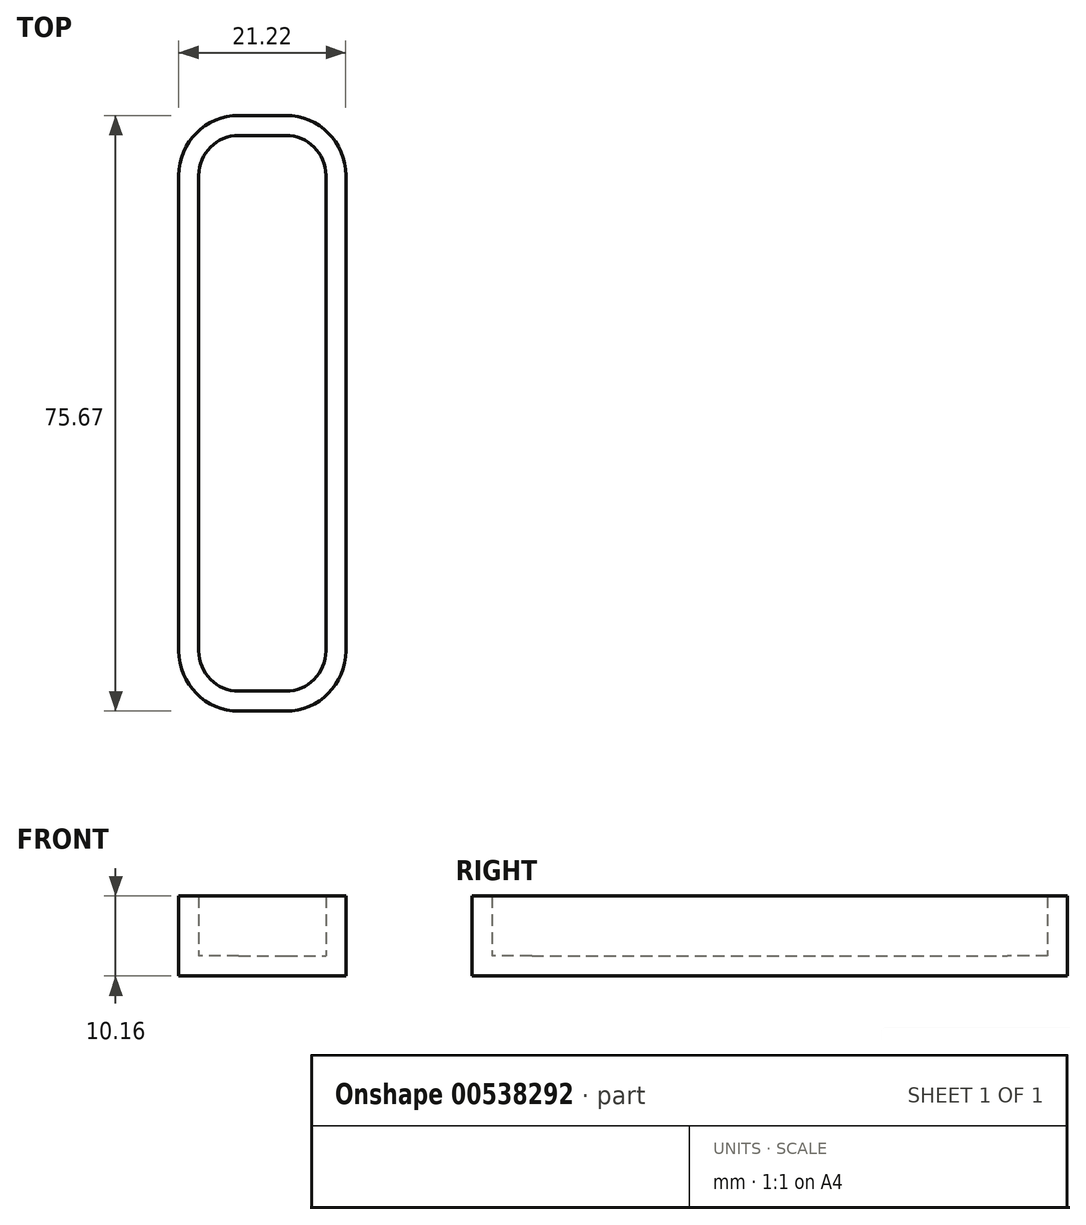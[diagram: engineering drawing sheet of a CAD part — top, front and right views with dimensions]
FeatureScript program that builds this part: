
annotation { "Feature Type Name" : "Feature", "Feature Type Description" : "" }
export const myFeature = defineFeature(function(context is Context, id is Id, definition is map)
    precondition{}
    {
        {
            var Q0;
            Q0=qCreatedBy(makeId("Top.planeOp"),FACE);
            var sketch = newSketch(context, id + "F0", { "sketchPlane" : qUnion([Q0])});
            skLineSegment(sketch, "E0.bottom", {"start": v(-143.26, -29.32) * mm, "end": v(-127.12, -29.32) * mm});
            skLineSegment(sketch, "E0.top", {"start": v(-143.26, 41.27) * mm, "end": v(-127.12, 41.27) * mm});
            skLineSegment(sketch, "E0.left", {"start": v(-143.26, -29.32) * mm, "end": v(-143.26, 41.27) * mm});
            skLineSegment(sketch, "E0.right", {"start": v(-127.12, -29.32) * mm, "end": v(-127.12, 41.27) * mm});
            skSolve(sketch);
        }
        {
            var Q0;
            Q0=makeQuery(id+"F0.imprint","IMPRINT",FACE,{"disambiguationData":[TD([[makeQuery(id+"F0.imprint","IMPRINT",EDGE,{"derivedFrom":sQuery(id+"F0.wireOp",EDGE,"E0.bottom")}),1.0]])]});
            extrude(context, id + "F1", {"entities" : qUnion([Q0]), "depth" : 7.62 * mm, "offsetDistance" : 25.4 * mm});
        }
        {
            var Q0;
            Q0=makeQuery(id+"F1.opExtrude","SWEPT_EDGE",EDGE,{"disambiguationData":[OSD([sQuery(id+"F0.wireOp",EDGE,"E0.bottom"),sQuery(id+"F0.wireOp",EDGE,"E0.left")])]});
            fillet(context, id + "F2", {"entities" : qUnion([Q0]), "radius" : 5.08 * mm, "tangentPropagation" : true, "allowEdgeOverflow" : false});
        }
        {
            var Q0;
            Q0=makeQuery(id+"F1.opExtrude","SWEPT_EDGE",EDGE,{"disambiguationData":[OSD([sQuery(id+"F0.wireOp",EDGE,"E0.bottom"),sQuery(id+"F0.wireOp",EDGE,"E0.right")])]});
            fillet(context, id + "F3", {"entities" : qUnion([Q0]), "radius" : 5.08 * mm, "tangentPropagation" : true, "allowEdgeOverflow" : false});
        }
        {
            var Q0;
            Q0=makeQuery(id+"F1.opExtrude","SWEPT_EDGE",EDGE,{"disambiguationData":[OSD([sQuery(id+"F0.wireOp",EDGE,"E0.top"),sQuery(id+"F0.wireOp",EDGE,"E0.left")])]});
            fillet(context, id + "F4", {"entities" : qUnion([Q0]), "radius" : 5.08 * mm, "tangentPropagation" : true, "allowEdgeOverflow" : false});
        }
        {
            var Q0;
            Q0=makeQuery(id+"F1.opExtrude","SWEPT_EDGE",EDGE,{"disambiguationData":[OSD([sQuery(id+"F0.wireOp",EDGE,"E0.top"),sQuery(id+"F0.wireOp",EDGE,"E0.right")])]});
            fillet(context, id + "F5", {"entities" : qUnion([Q0]), "radius" : 5.08 * mm, "tangentPropagation" : true, "allowEdgeOverflow" : false});
        }
        {
            var Q0;
            Q0=makeQuery(id+"F1.opExtrude","CAP_FACE",FACE,{"disambiguationData":[OSD([sQuery(id+"F0.wireOp",EDGE,"E0.bottom"),sQuery(id+"F0.wireOp",EDGE,"E0.top"),sQuery(id+"F0.wireOp",EDGE,"E0.left"),sQuery(id+"F0.wireOp",EDGE,"E0.right")])],"isStart":false});
            shell(context, id + "F6", {"entities" : qUnion([Q0]), "thickness" : 2.54 * mm, "oppositeDirection" : true});
        }
    });
